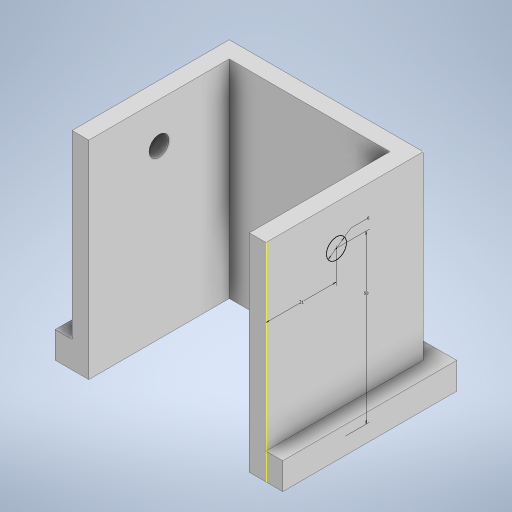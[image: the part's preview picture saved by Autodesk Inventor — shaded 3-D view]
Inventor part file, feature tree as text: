
AUTODESK INVENTOR PART (.ipt)
format: ipt  version: 2023 (Build 270158000, 158)  size: 269,312 bytes
history: native  units: in
note: dims shown in document units (in); Inventor stores cm internally (conversion verified against a paired STEP export)
features: sketch x5, extrude x4
ambient origin geometry x8: Origin, YZ Plane, XZ Plane, XY Plane, X Axis, Y Axis, Z Axis, Center Point
bodies: Solid1 (feature_tree)
feature tree (9):
  extrude  "Extrusion1"  Depth=0.1969in
  sketch  "Sketch2"  dims[d2=0.1969in d3=1.6535in]
  extrude  "Extrusion3"  Depth=1.6535in
  sketch  "Sketch4"  dims[d6=2.4409in d7=0.0in d8=0.8268in]
  extrude  "Extrusion5"  Depth=1.6535in
  extrude  "Extrusion6"  Depth=2.4409in
  sketch  "Sketch1"  dims[d0=2.2835in d1=0.1969in]
  sketch  "Sketch3"  dims[d4=0.1969in d5=1.6535in]
  sketch  "Sketch5"  dims[d9=1.9685in d10=0.2362in d13=0.1969in d14=0.1969in d15=0.1969in d16=0.315in d17=0.0in d18=0.3937in d19=0.3937in d20=0.1969in d21=0.1969in d25=0.1969in d26=0.0in d29=0.1969in d30=0.1969in d31=0.1969in d32=0.0in d11=0.0197in d12=0.0344in]
